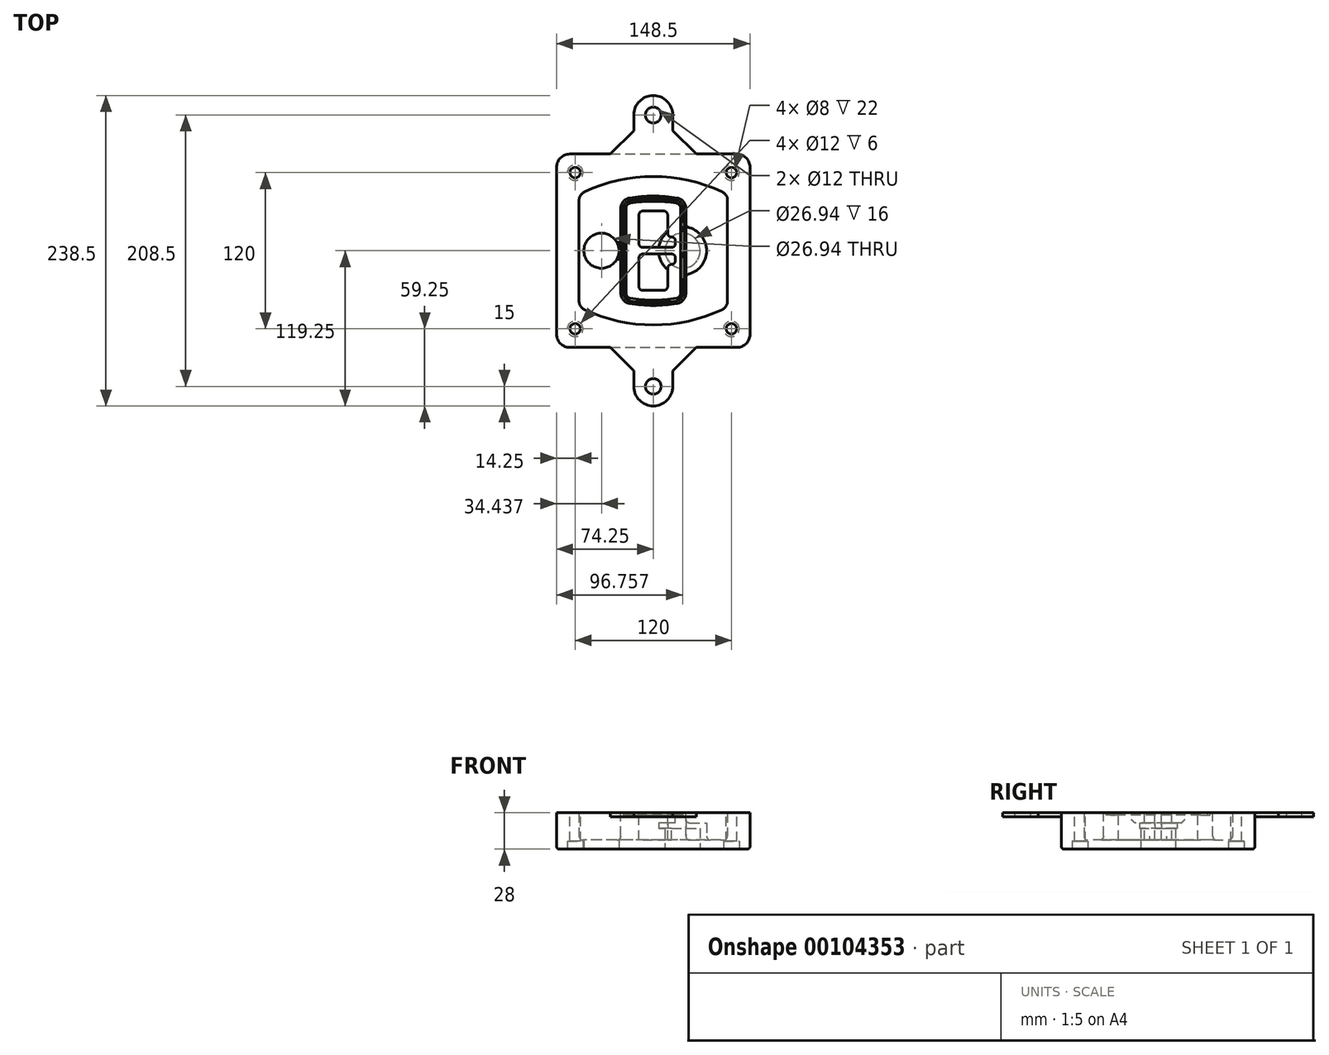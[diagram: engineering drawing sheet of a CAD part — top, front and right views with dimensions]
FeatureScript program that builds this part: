
annotation { "Feature Type Name" : "Feature", "Feature Type Description" : "" }
export const myFeature = defineFeature(function(context is Context, id is Id, definition is map)
    precondition{}
    {
        {
            var Q0;
            Q0=qCreatedBy(makeId("Top.planeOp"),FACE);
            var sketch = newSketch(context, id + "F0", { "sketchPlane" : qUnion([Q0])});
            skPoint(sketch, "E0.rect.middle", {"position": v(0, 0) * mm});
            skLineSegment(sketch, "E1.bottom", {"start": v(-64.25, -74.25) * mm, "end": v(64.25, -74.25) * mm});
            skLineSegment(sketch, "E1.top", {"start": v(-64.25, 74.25) * mm, "end": v(64.25, 74.25) * mm});
            skLineSegment(sketch, "E1.left", {"start": v(-74.25, -64.25) * mm, "end": v(-74.25, 64.25) * mm});
            skLineSegment(sketch, "E1.right", {"start": v(74.25, -64.25) * mm, "end": v(74.25, 64.25) * mm});
            skLineSegment(sketch, "E2", {"start": v(-74.25, 74.25) * mm, "end": v(74.25, -74.25) * mm, "construction": true});
            skLineSegment(sketch, "E3", {"start": v(74.25, 74.25) * mm, "end": v(-74.25, -74.25) * mm, "construction": true});
            skCircle(sketch, "E4", {"center": v(-60, 60) * mm, "radius": 4 * mm});
            skCircle(sketch, "E5", {"center": v(60, 60) * mm, "radius": 4 * mm});
            skCircle(sketch, "E6", {"center": v(60, -60) * mm, "radius": 4 * mm});
            skCircle(sketch, "E7", {"center": v(-60, -60) * mm, "radius": 4 * mm});
            skLineSegment(sketch, "E8", {"start": v(-60, 60) * mm, "end": v(60, 60) * mm, "construction": true});
            skLineSegment(sketch, "E9", {"start": v(60, 60) * mm, "end": v(60, -60) * mm, "construction": true});
            skLineSegment(sketch, "E10", {"start": v(60, -60) * mm, "end": v(-60, -60) * mm, "construction": true});
            skLineSegment(sketch, "E11", {"start": v(-60, -60) * mm, "end": v(-60, 60) * mm, "construction": true});
            skLineSegment(sketch, "E12", {"start": v(-60, 38.83) * mm, "end": v(-60, -38.83) * mm});
            skLineSegment(sketch, "E13", {"start": v(60, 38.83) * mm, "end": v(60, -38.83) * mm});
            skArc(sketch, "E14", {"start": v(54.26, 47.88) * mm, "mid": v(0, 60) * mm, "end": v(-54.26, 47.88) * mm});
            skArc(sketch, "E15", {"start": v(-54.26, -47.88) * mm, "mid": v(0, -60) * mm, "end": v(54.26, -47.88) * mm});
            skLineSegment(sketch, "E16", {"start": v(-60, 0) * mm, "end": v(60, 0) * mm, "construction": true});
            skPoint(sketch, "E17.visualSharp", {"position": v(-60, -45) * mm});
            skArc(sketch, "E17.filletArc", {"start": v(-60, -38.83) * mm, "mid": v(-58.44, -44.2) * mm, "end": v(-54.26, -47.88) * mm});
            skPoint(sketch, "E18.visualSharp", {"position": v(-60, 45) * mm});
            skArc(sketch, "E18.filletArc", {"start": v(-54.26, 47.88) * mm, "mid": v(-58.44, 44.2) * mm, "end": v(-60, 38.83) * mm});
            skPoint(sketch, "E19.visualSharp", {"position": v(60, 45) * mm});
            skArc(sketch, "E19.filletArc", {"start": v(60, 38.83) * mm, "mid": v(58.44, 44.2) * mm, "end": v(54.26, 47.88) * mm});
            skPoint(sketch, "E20.visualSharp", {"position": v(60, -45) * mm});
            skArc(sketch, "E20.filletArc", {"start": v(54.26, -47.88) * mm, "mid": v(58.44, -44.2) * mm, "end": v(60, -38.83) * mm});
            skPoint(sketch, "E21.visualSharp", {"position": v(-74.25, 74.25) * mm});
            skArc(sketch, "E21.filletArc", {"start": v(-64.25, 74.25) * mm, "mid": v(-71.32, 71.32) * mm, "end": v(-74.25, 64.25) * mm});
            skPoint(sketch, "E22.visualSharp", {"position": v(74.25, 74.25) * mm});
            skArc(sketch, "E22.filletArc", {"start": v(74.25, 64.25) * mm, "mid": v(71.32, 71.32) * mm, "end": v(64.25, 74.25) * mm});
            skPoint(sketch, "E23.visualSharp", {"position": v(74.25, -74.25) * mm});
            skArc(sketch, "E23.filletArc", {"start": v(64.25, -74.25) * mm, "mid": v(71.32, -71.32) * mm, "end": v(74.25, -64.25) * mm});
            skPoint(sketch, "E24.visualSharp", {"position": v(-74.25, -74.25) * mm});
            skArc(sketch, "E24.filletArc", {"start": v(-74.25, -64.25) * mm, "mid": v(-71.32, -71.32) * mm, "end": v(-64.25, -74.25) * mm});
            skArc(sketch, "E25.0", {"start": v(57, 38.83) * mm, "mid": v(55.9, 42.58) * mm, "end": v(52.98, 45.17) * mm});
            skLineSegment(sketch, "E25.1", {"start": v(57, 38.83) * mm, "end": v(57, -38.83) * mm});
            skArc(sketch, "E25.2", {"start": v(52.98, -45.17) * mm, "mid": v(55.9, -42.58) * mm, "end": v(57, -38.83) * mm});
            skArc(sketch, "E25.3", {"start": v(-52.98, -45.17) * mm, "mid": v(0, -57) * mm, "end": v(52.98, -45.17) * mm});
            skArc(sketch, "E25.4", {"start": v(-57, -38.83) * mm, "mid": v(-55.9, -42.58) * mm, "end": v(-52.98, -45.17) * mm});
            skArc(sketch, "E25.5", {"start": v(52.98, 45.17) * mm, "mid": v(0, 57) * mm, "end": v(-52.98, 45.17) * mm});
            skLineSegment(sketch, "E25.6", {"start": v(-57, 38.83) * mm, "end": v(-57, -38.83) * mm});
            skArc(sketch, "E25.7", {"start": v(-52.98, 45.17) * mm, "mid": v(-55.9, 42.58) * mm, "end": v(-57, 38.83) * mm});
            skArc(sketch, "E26.0", {"start": v(-55.96, 51.5) * mm, "mid": v(-61.82, 46.33) * mm, "end": v(-64, 38.83) * mm});
            skArc(sketch, "E26.1", {"start": v(55.96, 51.5) * mm, "mid": v(0, 64) * mm, "end": v(-55.96, 51.5) * mm});
            skArc(sketch, "E26.2", {"start": v(64, 38.83) * mm, "mid": v(61.82, 46.33) * mm, "end": v(55.96, 51.5) * mm});
            skLineSegment(sketch, "E26.3", {"start": v(64, 38.83) * mm, "end": v(64, -38.83) * mm});
            skArc(sketch, "E26.4", {"start": v(55.96, -51.5) * mm, "mid": v(61.82, -46.33) * mm, "end": v(64, -38.83) * mm});
            skLineSegment(sketch, "E26.5", {"start": v(-64, 38.83) * mm, "end": v(-64, -38.83) * mm});
            skArc(sketch, "E26.6", {"start": v(-55.96, -51.5) * mm, "mid": v(0, -64) * mm, "end": v(55.96, -51.5) * mm});
            skArc(sketch, "E26.7", {"start": v(-64, -38.83) * mm, "mid": v(-61.82, -46.33) * mm, "end": v(-55.96, -51.5) * mm});
            skSolve(sketch);
        }
        {
            var Q0;
            Q0=makeQuery(id+"F0.imprint","IMPRINT",FACE,{"disambiguationData":[TD([[makeQuery(id+"F0.imprint","IMPRINT",EDGE,{"derivedFrom":sQuery(id+"F0.wireOp",EDGE,"E1.bottom")}),1.0]])]});
            var Q1;
            Q1=makeQuery(id+"F0.imprint","IMPRINT",FACE,{"disambiguationData":[TD([[makeQuery(id+"F0.imprint","IMPRINT",EDGE,{"derivedFrom":sQuery(id+"F0.wireOp",EDGE,"E12")}),1.0]])]});
            var Q2;
            Q2=makeQuery(id+"F0.imprint","IMPRINT",FACE,{"disambiguationData":[TD([[makeQuery(id+"F0.imprint","IMPRINT",EDGE,{"derivedFrom":sQuery(id+"F0.wireOp",EDGE,"E25.0")}),1.0]])]});
            var Q3;
            Q3=makeQuery(id+"F0.imprint","IMPRINT",FACE,{"disambiguationData":[TD([[makeQuery(id+"F0.imprint","IMPRINT",EDGE,{"derivedFrom":sQuery(id+"F0.wireOp",EDGE,"E12")}),-1.0]])]});
            extrude(context, id + "F1", {"entities" : qUnion([Q0, Q1, Q2, Q3]), "oppositeDirection" : true, "depth" : 25 * mm});
        }
        {
            var Q0;
            Q0=makeQuery(id+"F0.imprint","IMPRINT",FACE,{"disambiguationData":[TD([[makeQuery(id+"F0.imprint","IMPRINT",EDGE,{"derivedFrom":sQuery(id+"F0.wireOp",EDGE,"E12")}),1.0]])]});
            extrude(context, id + "F2", {"entities" : qUnion([Q0]), "operationType" : NewBodyOperationType.ADD, "depth" : 3 * mm});
        }
        {
            var Q0;
            Q0=makeQuery(id+"F0.imprint","IMPRINT",FACE,{"disambiguationData":[TD([[makeQuery(id+"F0.imprint","IMPRINT",EDGE,{"derivedFrom":sQuery(id+"F0.wireOp",EDGE,"E25.0")}),1.0]])]});
            extrude(context, id + "F3", {"entities" : qUnion([Q0]), "operationType" : NewBodyOperationType.REMOVE, "oppositeDirection" : true, "depth" : 18 * mm});
        }
        {
            var Q0;
            Q0=makeQuery(id+"F2.opExtrude","CAP_FACE",FACE,{"disambiguationData":[OSD([sQuery(id+"F0.wireOp",EDGE,"E12"),sQuery(id+"F0.wireOp",EDGE,"E13"),sQuery(id+"F0.wireOp",EDGE,"E14"),sQuery(id+"F0.wireOp",EDGE,"E15"),sQuery(id+"F0.wireOp",EDGE,"E17.filletArc"),sQuery(id+"F0.wireOp",EDGE,"E18.filletArc"),sQuery(id+"F0.wireOp",EDGE,"E19.filletArc"),sQuery(id+"F0.wireOp",EDGE,"E20.filletArc"),sQuery(id+"F0.wireOp",EDGE,"E25.0"),sQuery(id+"F0.wireOp",EDGE,"E25.1"),sQuery(id+"F0.wireOp",EDGE,"E25.2"),sQuery(id+"F0.wireOp",EDGE,"E25.3"),sQuery(id+"F0.wireOp",EDGE,"E25.4"),sQuery(id+"F0.wireOp",EDGE,"E25.5"),sQuery(id+"F0.wireOp",EDGE,"E25.6"),sQuery(id+"F0.wireOp",EDGE,"E25.7")])],"isStart":false});
            var sketch = newSketch(context, id + "F4", { "sketchPlane" : qUnion([Q0])});
            skArc(sketch, "E27.0", {"start": v(-18.34, -40.45) * mm, "mid": v(0, -42) * mm, "end": v(18.34, -40.45) * mm});
            skArc(sketch, "E28.0", {"start": v(18.34, 40.45) * mm, "mid": v(0, 42) * mm, "end": v(-18.34, 40.45) * mm});
            skLineSegment(sketch, "E29", {"start": v(-25, 32.57) * mm, "end": v(-25, -32.57) * mm});
            skLineSegment(sketch, "E30", {"start": v(25, 32.57) * mm, "end": v(25, -32.57) * mm});
            skLineSegment(sketch, "E31", {"start": v(-25, 39.1) * mm, "end": v(25, 39.1) * mm, "construction": true});
            skLineSegment(sketch, "E32", {"start": v(-25, -39.1) * mm, "end": v(25, -39.1) * mm, "construction": true});
            skPoint(sketch, "E33.visualSharp", {"position": v(-25, 39.1) * mm});
            skArc(sketch, "E33.filletArc", {"start": v(-18.34, 40.45) * mm, "mid": v(-23.11, 37.73) * mm, "end": v(-25, 32.57) * mm});
            skPoint(sketch, "E34.visualSharp", {"position": v(25, 39.1) * mm});
            skArc(sketch, "E34.filletArc", {"start": v(25, 32.57) * mm, "mid": v(23.11, 37.73) * mm, "end": v(18.34, 40.45) * mm});
            skPoint(sketch, "E35.visualSharp", {"position": v(25, -39.1) * mm});
            skArc(sketch, "E35.filletArc", {"start": v(18.34, -40.45) * mm, "mid": v(23.11, -37.73) * mm, "end": v(25, -32.57) * mm});
            skPoint(sketch, "E36.visualSharp", {"position": v(-25, -39.1) * mm});
            skArc(sketch, "E36.filletArc", {"start": v(-25, -32.57) * mm, "mid": v(-23.11, -37.73) * mm, "end": v(-18.34, -40.45) * mm});
            skArc(sketch, "E37.0", {"start": v(52.98, 45.17) * mm, "mid": v(0, 57) * mm, "end": v(-52.98, 45.17) * mm});
            skArc(sketch, "E37.1", {"start": v(-52.98, 45.17) * mm, "mid": v(-55.9, 42.58) * mm, "end": v(-57, 38.83) * mm});
            skLineSegment(sketch, "E37.2", {"start": v(-57, 38.83) * mm, "end": v(-57, -38.83) * mm});
            skArc(sketch, "E37.3", {"start": v(-57, -38.83) * mm, "mid": v(-55.9, -42.58) * mm, "end": v(-52.98, -45.17) * mm});
            skArc(sketch, "E37.4", {"start": v(-52.98, -45.17) * mm, "mid": v(0, -57) * mm, "end": v(52.98, -45.17) * mm});
            skArc(sketch, "E37.5", {"start": v(52.98, -45.17) * mm, "mid": v(55.9, -42.58) * mm, "end": v(57, -38.83) * mm});
            skLineSegment(sketch, "E37.6", {"start": v(57, 38.83) * mm, "end": v(57, -38.83) * mm});
            skArc(sketch, "E37.7", {"start": v(57, 38.83) * mm, "mid": v(55.9, 42.58) * mm, "end": v(52.98, 45.17) * mm});
            skLineSegment(sketch, "E38.0", {"start": v(23, 32.57) * mm, "end": v(23, -32.57) * mm});
            skArc(sketch, "E38.1", {"start": v(18, -38.48) * mm, "mid": v(21.58, -36.44) * mm, "end": v(23, -32.57) * mm});
            skArc(sketch, "E38.2", {"start": v(-18, -38.48) * mm, "mid": v(0, -40) * mm, "end": v(18, -38.48) * mm});
            skArc(sketch, "E38.3", {"start": v(-23, -32.57) * mm, "mid": v(-21.58, -36.44) * mm, "end": v(-18, -38.48) * mm});
            skLineSegment(sketch, "E38.4", {"start": v(-23, 32.57) * mm, "end": v(-23, -32.57) * mm});
            skArc(sketch, "E38.5", {"start": v(23, 32.57) * mm, "mid": v(21.58, 36.44) * mm, "end": v(18, 38.48) * mm});
            skArc(sketch, "E38.6", {"start": v(-18, 38.48) * mm, "mid": v(-21.58, 36.44) * mm, "end": v(-23, 32.57) * mm});
            skArc(sketch, "E38.7", {"start": v(18, 38.48) * mm, "mid": v(0, 40) * mm, "end": v(-18, 38.48) * mm});
            skArc(sketch, "E39.0", {"start": v(21, 32.57) * mm, "mid": v(20.06, 35.15) * mm, "end": v(17.67, 36.5) * mm});
            skLineSegment(sketch, "E39.1", {"start": v(21, 32.57) * mm, "end": v(21, -32.57) * mm});
            skArc(sketch, "E39.2", {"start": v(17.67, -36.5) * mm, "mid": v(20.06, -35.15) * mm, "end": v(21, -32.57) * mm});
            skArc(sketch, "E39.3", {"start": v(-17.67, -36.5) * mm, "mid": v(0, -38) * mm, "end": v(17.67, -36.5) * mm});
            skArc(sketch, "E39.4", {"start": v(-21, -32.57) * mm, "mid": v(-20.06, -35.15) * mm, "end": v(-17.67, -36.5) * mm});
            skArc(sketch, "E39.5", {"start": v(17.67, 36.5) * mm, "mid": v(0, 38) * mm, "end": v(-17.67, 36.5) * mm});
            skLineSegment(sketch, "E39.6", {"start": v(-21, 32.57) * mm, "end": v(-21, -32.57) * mm});
            skArc(sketch, "E39.7", {"start": v(-17.67, 36.5) * mm, "mid": v(-20.06, 35.15) * mm, "end": v(-21, 32.57) * mm});
            skLineSegment(sketch, "E40", {"start": v(-25, 0) * mm, "end": v(25, 0) * mm, "construction": true});
            skLineSegment(sketch, "E41", {"start": v(-11, 5.5) * mm, "end": v(-11, 27.5) * mm});
            skLineSegment(sketch, "E42", {"start": v(-8, 30.5) * mm, "end": v(8, 30.5) * mm});
            skLineSegment(sketch, "E43", {"start": v(11, 27.5) * mm, "end": v(11, 13.5) * mm});
            skLineSegment(sketch, "E44", {"start": v(14, 10.5) * mm, "end": v(14, 10.5) * mm});
            skLineSegment(sketch, "E45", {"start": v(17, 7.5) * mm, "end": v(17, 5.5) * mm});
            skLineSegment(sketch, "E46", {"start": v(14, 2.5) * mm, "end": v(-8, 2.5) * mm});
            skPoint(sketch, "E47.visualSharp", {"position": v(-11, 30.5) * mm});
            skArc(sketch, "E47.filletArc", {"start": v(-8, 30.5) * mm, "mid": v(-10.12, 29.62) * mm, "end": v(-11, 27.5) * mm});
            skPoint(sketch, "E48.visualSharp", {"position": v(11, 30.5) * mm});
            skArc(sketch, "E48.filletArc", {"start": v(11, 27.5) * mm, "mid": v(10.12, 29.62) * mm, "end": v(8, 30.5) * mm});
            skPoint(sketch, "E49.visualSharp", {"position": v(11, 10.5) * mm});
            skArc(sketch, "E49.filletArc", {"start": v(11, 13.5) * mm, "mid": v(11.88, 11.38) * mm, "end": v(14, 10.5) * mm});
            skPoint(sketch, "E50.visualSharp", {"position": v(17, 10.5) * mm});
            skArc(sketch, "E50.filletArc", {"start": v(17, 7.5) * mm, "mid": v(16.12, 9.62) * mm, "end": v(14, 10.5) * mm});
            skPoint(sketch, "E51.visualSharp", {"position": v(17, 2.5) * mm});
            skArc(sketch, "E51.filletArc", {"start": v(14, 2.5) * mm, "mid": v(16.12, 3.38) * mm, "end": v(17, 5.5) * mm});
            skPoint(sketch, "E52.visualSharp", {"position": v(-11, 2.5) * mm});
            skArc(sketch, "E52.filletArc", {"start": v(-11, 5.5) * mm, "mid": v(-10.12, 3.38) * mm, "end": v(-8, 2.5) * mm});
            skLineSegment(sketch, "E53.0.MirrorCS", {"start": v(14, -2.5) * mm, "end": v(-8, -2.5) * mm});
            skArc(sketch, "E54.0.MirrorCS", {"start": v(-11, -5.5) * mm, "mid": v(-10.12, -3.38) * mm, "end": v(-8, -2.5) * mm});
            skLineSegment(sketch, "E55.0.MirrorCS", {"start": v(-11, -5.5) * mm, "end": v(-11, -27.5) * mm});
            skArc(sketch, "E56.0.MirrorCS", {"start": v(-8, -30.5) * mm, "mid": v(-10.12, -29.62) * mm, "end": v(-11, -27.5) * mm});
            skLineSegment(sketch, "E57.0.MirrorCS", {"start": v(-8, -30.5) * mm, "end": v(8, -30.5) * mm});
            skArc(sketch, "E58.0.MirrorCS", {"start": v(11, -27.5) * mm, "mid": v(10.12, -29.62) * mm, "end": v(8, -30.5) * mm});
            skLineSegment(sketch, "E59.0.MirrorCS", {"start": v(11, -27.5) * mm, "end": v(11, -13.5) * mm});
            skArc(sketch, "E60.0.MirrorCS", {"start": v(11, -13.5) * mm, "mid": v(11.88, -11.38) * mm, "end": v(14, -10.5) * mm});
            skArc(sketch, "E61.0.MirrorCS", {"start": v(17, -7.5) * mm, "mid": v(16.12, -9.62) * mm, "end": v(14, -10.5) * mm});
            skLineSegment(sketch, "E62.0.MirrorCS", {"start": v(17, -7.5) * mm, "end": v(17, -5.5) * mm});
            skArc(sketch, "E63.0.MirrorCS", {"start": v(14, -2.5) * mm, "mid": v(16.12, -3.38) * mm, "end": v(17, -5.5) * mm});
            skSolve(sketch);
        }
        {
            var Q0;
            Q0=makeQuery(id+"F4.imprint","IMPRINT",FACE,{"disambiguationData":[TD([[makeQuery(id+"F4.imprint","IMPRINT",EDGE,{"derivedFrom":sQuery(id+"F4.wireOp",EDGE,"E27.0")}),1.0]])]});
            var Q1;
            Q1=makeQuery(id+"F4.imprint","IMPRINT",FACE,{"disambiguationData":[TD([[makeQuery(id+"F4.imprint","IMPRINT",EDGE,{"derivedFrom":sQuery(id+"F4.wireOp",EDGE,"E38.0")}),-1.0]])]});
            var Q2;
            Q2=makeQuery(id+"F4.imprint","IMPRINT",FACE,{"disambiguationData":[TD([[makeQuery(id+"F4.imprint","IMPRINT",EDGE,{"derivedFrom":sQuery(id+"F4.wireOp",EDGE,"E39.0")}),1.0]])]});
            extrude(context, id + "F5", {"entities" : qUnion([Q0, Q1, Q2]), "operationType" : NewBodyOperationType.ADD, "endBound" : BoundingType.UP_TO_NEXT, "oppositeDirection" : true, "depth" : 25 * mm});
        }
        {
            var Q0;
            Q0=makeQuery(id+"F4.imprint","IMPRINT",FACE,{"disambiguationData":[TD([[makeQuery(id+"F4.imprint","IMPRINT",EDGE,{"derivedFrom":sQuery(id+"F4.wireOp",EDGE,"E38.0")}),-1.0]])]});
            extrude(context, id + "F6", {"entities" : qUnion([Q0]), "operationType" : NewBodyOperationType.REMOVE, "oppositeDirection" : true, "depth" : 2 * mm});
        }
        {
            var Q0;
            Q0=makeQuery(id+"F1.opExtrude","CAP_FACE",FACE,{"disambiguationData":[OSD([sQuery(id+"F0.wireOp",EDGE,"E1.bottom"),sQuery(id+"F0.wireOp",EDGE,"E1.top"),sQuery(id+"F0.wireOp",EDGE,"E1.left"),sQuery(id+"F0.wireOp",EDGE,"E1.right"),sQuery(id+"F0.wireOp",EDGE,"E4"),sQuery(id+"F0.wireOp",EDGE,"E5"),sQuery(id+"F0.wireOp",EDGE,"E6"),sQuery(id+"F0.wireOp",EDGE,"E7"),sQuery(id+"F0.wireOp",EDGE,"E21.filletArc"),sQuery(id+"F0.wireOp",EDGE,"E22.filletArc"),sQuery(id+"F0.wireOp",EDGE,"E23.filletArc"),sQuery(id+"F0.wireOp",EDGE,"E24.filletArc")])],"isStart":false});
            var sketch = newSketch(context, id + "F7", { "sketchPlane" : qUnion([Q0])});
            skCircle(sketch, "E64", {"center": v(22.5, 0) * mm, "radius": 13.47 * mm});
            skCircle(sketch, "E65", {"center": v(-39.81, 0) * mm, "radius": 13.47 * mm});
            skLineSegment(sketch, "E66", {"start": v(74.25, 0) * mm, "end": v(-74.25, 0) * mm});
            skCircle(sketch, "E67", {"center": v(22.5, 0) * mm, "radius": 18.47 * mm});
            skCircle(sketch, "E68", {"center": v(60, -60) * mm, "radius": 6 * mm});
            skCircle(sketch, "E69", {"center": v(-60, -60) * mm, "radius": 6 * mm});
            skCircle(sketch, "E70", {"center": v(-60, 60) * mm, "radius": 6 * mm});
            skCircle(sketch, "E71", {"center": v(60, 60) * mm, "radius": 6 * mm});
            skSolve(sketch);
        }
        {
            var Q0;
            {var subQ1=sQuery(id+"F7.wireOp",EDGE,"E66");var subQ4=sQuery(id+"F7.wireOp",EDGE,"E64");var subQ6=makeQuery(id+"F7.imprint","INTERSECT",VERTEX,{"disambiguationData":[OD(0.0)],"derivedFrom":[subQ4,subQ1]});Q0=makeQuery(id+"F7.imprint","IMPRINT",FACE,{"disambiguationData":[TD([[makeQuery(id+"F7.imprint","IMPRINT",EDGE,{"disambiguationData":[TD([[subQ6,-1.0]])],"derivedFrom":subQ4}),-1.0]])]});}
            var Q1;
            {var subQ0=sQuery(id+"F7.wireOp",EDGE,"E66");var subQ1=sQuery(id+"F7.wireOp",EDGE,"E64");var subQ3=makeQuery(id+"F7.imprint","INTERSECT",VERTEX,{"disambiguationData":[OD(0.0)],"derivedFrom":[subQ1,subQ0]});Q1=makeQuery(id+"F7.imprint","IMPRINT",FACE,{"disambiguationData":[TD([[makeQuery(id+"F7.imprint","IMPRINT",EDGE,{"disambiguationData":[TD([[subQ3,-1.0]])],"derivedFrom":subQ1}),1.0]])]});}
            var Q2;
            {var subQ0=sQuery(id+"F7.wireOp",EDGE,"E66");var subQ1=sQuery(id+"F7.wireOp",EDGE,"E64");var subQ3=makeQuery(id+"F7.imprint","INTERSECT",VERTEX,{"disambiguationData":[OD(0.0)],"derivedFrom":[subQ1,subQ0]});Q2=makeQuery(id+"F7.imprint","IMPRINT",FACE,{"disambiguationData":[TD([[makeQuery(id+"F7.imprint","IMPRINT",EDGE,{"disambiguationData":[TD([[subQ3,1.0]])],"derivedFrom":subQ1}),1.0]])]});}
            var Q3;
            {var subQ1=sQuery(id+"F7.wireOp",EDGE,"E66");var subQ4=sQuery(id+"F7.wireOp",EDGE,"E64");var subQ6=makeQuery(id+"F7.imprint","INTERSECT",VERTEX,{"disambiguationData":[OD(0.0)],"derivedFrom":[subQ4,subQ1]});Q3=makeQuery(id+"F7.imprint","IMPRINT",FACE,{"disambiguationData":[TD([[makeQuery(id+"F7.imprint","IMPRINT",EDGE,{"disambiguationData":[TD([[subQ6,1.0]])],"derivedFrom":subQ4}),-1.0]])]});}
            extrude(context, id + "F8", {"entities" : qUnion([Q0, Q1, Q2, Q3]), "operationType" : NewBodyOperationType.ADD, "oppositeDirection" : true, "depth" : 20 * mm});
        }
        {
            var Q0;
            {var subQ0=sQuery(id+"F7.wireOp",EDGE,"E66");var subQ1=sQuery(id+"F7.wireOp",EDGE,"E64");var subQ3=makeQuery(id+"F7.imprint","INTERSECT",VERTEX,{"disambiguationData":[OD(0.0)],"derivedFrom":[subQ1,subQ0]});Q0=makeQuery(id+"F7.imprint","IMPRINT",FACE,{"disambiguationData":[TD([[makeQuery(id+"F7.imprint","IMPRINT",EDGE,{"disambiguationData":[TD([[subQ3,-1.0]])],"derivedFrom":subQ1}),1.0]])]});}
            var Q1;
            {var subQ0=sQuery(id+"F7.wireOp",EDGE,"E66");var subQ1=sQuery(id+"F7.wireOp",EDGE,"E64");var subQ3=makeQuery(id+"F7.imprint","INTERSECT",VERTEX,{"disambiguationData":[OD(0.0)],"derivedFrom":[subQ1,subQ0]});Q1=makeQuery(id+"F7.imprint","IMPRINT",FACE,{"disambiguationData":[TD([[makeQuery(id+"F7.imprint","IMPRINT",EDGE,{"disambiguationData":[TD([[subQ3,1.0]])],"derivedFrom":subQ1}),1.0]])]});}
            extrude(context, id + "F9", {"entities" : qUnion([Q0, Q1]), "operationType" : NewBodyOperationType.REMOVE, "oppositeDirection" : true, "depth" : 16 * mm});
        }
        {
            var Q0;
            {var subQ0=sQuery(id+"F7.wireOp",EDGE,"E66");var subQ1=sQuery(id+"F7.wireOp",EDGE,"E65");var subQ3=makeQuery(id+"F7.imprint","INTERSECT",VERTEX,{"disambiguationData":[OD(0.0)],"derivedFrom":[subQ1,subQ0]});Q0=makeQuery(id+"F7.imprint","IMPRINT",FACE,{"disambiguationData":[TD([[makeQuery(id+"F7.imprint","IMPRINT",EDGE,{"disambiguationData":[TD([[subQ3,-1.0]])],"derivedFrom":subQ1}),1.0]])]});}
            var Q1;
            {var subQ0=sQuery(id+"F7.wireOp",EDGE,"E66");var subQ1=sQuery(id+"F7.wireOp",EDGE,"E65");var subQ3=makeQuery(id+"F7.imprint","INTERSECT",VERTEX,{"disambiguationData":[OD(0.0)],"derivedFrom":[subQ1,subQ0]});Q1=makeQuery(id+"F7.imprint","IMPRINT",FACE,{"disambiguationData":[TD([[makeQuery(id+"F7.imprint","IMPRINT",EDGE,{"disambiguationData":[TD([[subQ3,1.0]])],"derivedFrom":subQ1}),1.0]])]});}
            extrude(context, id + "F10", {"entities" : qUnion([Q0, Q1]), "operationType" : NewBodyOperationType.REMOVE, "oppositeDirection" : true, "depth" : 25 * mm});
        }
        {
            var Q0;
            Q0=makeQuery(id+"F7.imprint","IMPRINT",FACE,{"disambiguationData":[TD([[makeQuery(id+"F7.imprint","IMPRINT",EDGE,{"derivedFrom":sQuery(id+"F7.wireOp",EDGE,"E68")}),1.0]])]});
            var Q1;
            Q1=makeQuery(id+"F7.imprint","IMPRINT",FACE,{"disambiguationData":[TD([[makeQuery(id+"F7.imprint","IMPRINT",EDGE,{"derivedFrom":makeQuery(id+"F1.opExtrude","CAP_EDGE",EDGE,{"disambiguationData":[OSD([sQuery(id+"F0.wireOp",EDGE,"E5")])],"isStart":false})}),-1.0]])]});
            var Q2;
            Q2=makeQuery(id+"F7.imprint","IMPRINT",FACE,{"disambiguationData":[TD([[makeQuery(id+"F7.imprint","IMPRINT",EDGE,{"derivedFrom":sQuery(id+"F7.wireOp",EDGE,"E69")}),1.0]])]});
            var Q3;
            Q3=makeQuery(id+"F7.imprint","IMPRINT",FACE,{"disambiguationData":[TD([[makeQuery(id+"F7.imprint","IMPRINT",EDGE,{"derivedFrom":makeQuery(id+"F1.opExtrude","CAP_EDGE",EDGE,{"disambiguationData":[OSD([sQuery(id+"F0.wireOp",EDGE,"E4")])],"isStart":false})}),-1.0]])]});
            var Q4;
            Q4=makeQuery(id+"F7.imprint","IMPRINT",FACE,{"disambiguationData":[TD([[makeQuery(id+"F7.imprint","IMPRINT",EDGE,{"derivedFrom":sQuery(id+"F7.wireOp",EDGE,"E70")}),1.0]])]});
            var Q5;
            Q5=makeQuery(id+"F7.imprint","IMPRINT",FACE,{"disambiguationData":[TD([[makeQuery(id+"F7.imprint","IMPRINT",EDGE,{"derivedFrom":makeQuery(id+"F1.opExtrude","CAP_EDGE",EDGE,{"disambiguationData":[OSD([sQuery(id+"F0.wireOp",EDGE,"E7")])],"isStart":false})}),-1.0]])]});
            var Q6;
            Q6=makeQuery(id+"F7.imprint","IMPRINT",FACE,{"disambiguationData":[TD([[makeQuery(id+"F7.imprint","IMPRINT",EDGE,{"derivedFrom":sQuery(id+"F7.wireOp",EDGE,"E71")}),1.0]])]});
            var Q7;
            Q7=makeQuery(id+"F7.imprint","IMPRINT",FACE,{"disambiguationData":[TD([[makeQuery(id+"F7.imprint","IMPRINT",EDGE,{"derivedFrom":makeQuery(id+"F1.opExtrude","CAP_EDGE",EDGE,{"disambiguationData":[OSD([sQuery(id+"F0.wireOp",EDGE,"E6")])],"isStart":false})}),-1.0]])]});
            extrude(context, id + "F11", {"entities" : qUnion([Q0, Q1, Q2, Q3, Q4, Q5, Q6, Q7]), "operationType" : NewBodyOperationType.REMOVE, "oppositeDirection" : true, "depth" : 6 * mm});
        }
        {
            var Q0;
            Q0=makeQuery(id+"F9.boolean.opBoolean","COPY",FACE,{"derivedFrom":makeQuery(id+"F9.opExtrude","CAP_FACE",FACE,{"disambiguationData":[OSD([sQuery(id+"F7.wireOp",EDGE,"E64")])],"isStart":false})});
            var sketch = newSketch(context, id + "F12", { "sketchPlane" : qUnion([Q0])});
            skArc(sketch, "E72.0", {"start": v(11, 14.45) * mm, "mid": v(6.45, 9.13) * mm, "end": v(4.2, 2.5) * mm});
            skArc(sketch, "E72.1", {"start": v(4.2, -2.5) * mm, "mid": v(6.45, -9.13) * mm, "end": v(11, -14.45) * mm});
            skLineSegment(sketch, "E73", {"start": v(4.2, -2.5) * mm, "end": v(14, -2.5) * mm});
            skLineSegment(sketch, "E74.0", {"start": v(14, 2.5) * mm, "end": v(4.2, 2.5) * mm});
            skArc(sketch, "E74.1", {"start": v(14, 2.5) * mm, "mid": v(16.12, 3.38) * mm, "end": v(17, 5.5) * mm});
            skLineSegment(sketch, "E74.2", {"start": v(17, 7.5) * mm, "end": v(17, 5.5) * mm});
            skArc(sketch, "E74.3", {"start": v(17, 7.5) * mm, "mid": v(16.12, 9.62) * mm, "end": v(14, 10.5) * mm});
            skArc(sketch, "E74.4", {"start": v(11, 13.5) * mm, "mid": v(11.88, 11.38) * mm, "end": v(14, 10.5) * mm});
            skLineSegment(sketch, "E74.5", {"start": v(11, 14.45) * mm, "end": v(11, 13.5) * mm});
            skLineSegment(sketch, "E74.7", {"start": v(14, -2.5) * mm, "end": v(4.2, -2.5) * mm});
            skArc(sketch, "E74.8", {"start": v(14, -2.5) * mm, "mid": v(16.12, -3.38) * mm, "end": v(17, -5.5) * mm});
            skLineSegment(sketch, "E74.9", {"start": v(17, -7.5) * mm, "end": v(17, -5.5) * mm});
            skArc(sketch, "E74.10", {"start": v(17, -7.5) * mm, "mid": v(16.12, -9.62) * mm, "end": v(14, -10.5) * mm});
            skArc(sketch, "E74.11", {"start": v(11, -13.5) * mm, "mid": v(11.88, -11.38) * mm, "end": v(14, -10.5) * mm});
            skLineSegment(sketch, "E74.12", {"start": v(11, -14.45) * mm, "end": v(11, -13.5) * mm});
            skPoint(sketch, "E75.orphan", {"position": v(11, -27.5) * mm});
            skPoint(sketch, "E76.orphan", {"position": v(-8, -2.5) * mm});
            skPoint(sketch, "E77.orphan", {"position": v(-8, 2.5) * mm});
            skPoint(sketch, "E78.orphan", {"position": v(11, 27.5) * mm});
            skSolve(sketch);
        }
        {
            var Q0;
            {var subQ7=sQuery(id+"F12.wireOp",EDGE,"E72.0");var subQ14=sQuery(id+"F12.wireOp",EDGE,"E72.1");var subQ16=sQuery(id+"F12.wireOp",EDGE,"E74.1");var subQ18=sQuery(id+"F12.wireOp",EDGE,"E74.8");Q0=qUnion([makeQuery(id+"F12.imprint","IMPRINT",FACE,{"disambiguationData":[TD([[makeQuery(id+"F12.imprint","IMPRINT",EDGE,{"derivedFrom":subQ7}),1.0]])]}),makeQuery(id+"F12.imprint","IMPRINT",FACE,{"disambiguationData":[TD([[makeQuery(id+"F12.imprint","IMPRINT",EDGE,{"derivedFrom":subQ14}),1.0]])]}),makeQuery(id+"F12.imprint","IMPRINT",FACE,{"disambiguationData":[TD([[makeQuery(id+"F12.imprint","IMPRINT",EDGE,{"derivedFrom":subQ16}),1.0]])]}),makeQuery(id+"F12.imprint","IMPRINT",FACE,{"disambiguationData":[TD([[makeQuery(id+"F12.imprint","IMPRINT",EDGE,{"derivedFrom":subQ18}),-1.0]])]})]);}
            var Q1;
            Q1=makeQuery(id+"F5.boolean.opBoolean","SPLIT",FACE,{"disambiguationData":[TD([makeQuery(id+"F5.opExtrude","SWEPT_FACE",FACE,{"disambiguationData":[OSD([sQuery(id+"F4.wireOp",EDGE,"E41")])]})])],"derivedFrom":makeQuery(id+"F3.boolean.opBoolean","COPY",FACE,{"derivedFrom":makeQuery(id+"F3.opExtrude","CAP_FACE",FACE,{"disambiguationData":[OSD([sQuery(id+"F0.wireOp",EDGE,"E25.0"),sQuery(id+"F0.wireOp",EDGE,"E25.1"),sQuery(id+"F0.wireOp",EDGE,"E25.2"),sQuery(id+"F0.wireOp",EDGE,"E25.3"),sQuery(id+"F0.wireOp",EDGE,"E25.4"),sQuery(id+"F0.wireOp",EDGE,"E25.5"),sQuery(id+"F0.wireOp",EDGE,"E25.6"),sQuery(id+"F0.wireOp",EDGE,"E25.7")])],"isStart":false})})});
            extrude(context, id + "F13", {"entities" : qUnion([Q0]), "operationType" : NewBodyOperationType.REMOVE, "endBound" : BoundingType.UP_TO_SURFACE, "endBoundEntityFace" : qUnion([Q1]), "depth" : 25 * mm});
        }
        {
            var Q0;
            Q0=makeQuery(id+"F3.boolean.opBoolean","COPY",EDGE,{"derivedFrom":makeQuery(id+"F3.opExtrude","CAP_EDGE",EDGE,{"disambiguationData":[OSD([sQuery(id+"F0.wireOp",EDGE,"E25.6")])],"isStart":false})});
            var Q1;
            Q1=makeQuery(id+"F8.boolean.opBoolean","INTERSECT",EDGE,{"derivedFrom":[makeQuery(id+"F5.opExtrude","SWEPT_FACE",FACE,{"disambiguationData":[OSD([sQuery(id+"F4.wireOp",EDGE,"E30")])]}),makeQuery(id+"F8.opExtrude","CAP_FACE",FACE,{"disambiguationData":[OSD([sQuery(id+"F7.wireOp",EDGE,"E67")])],"isStart":false})]});
            var Q2;
            Q2=makeQuery(id+"F8.boolean.opBoolean","INTERSECT",EDGE,{"disambiguationData":[OD(1.0)],"derivedFrom":[makeQuery(id+"F5.opExtrude","SWEPT_FACE",FACE,{"disambiguationData":[OSD([sQuery(id+"F4.wireOp",EDGE,"E30")])]}),makeQuery(id+"F8.opExtrude","SWEPT_FACE",FACE,{"disambiguationData":[OSD([sQuery(id+"F7.wireOp",EDGE,"E67")])]})]});
            var Q3;
            {var subQ0=sQuery(id+"F4.wireOp",EDGE,"E30");Q3=makeQuery(id+"F8.boolean.opBoolean","SPLIT",EDGE,{"disambiguationData":[TD([makeQuery(id+"F5.opExtrude","SWEPT_FACE",FACE,{"disambiguationData":[OSD([sQuery(id+"F4.wireOp",EDGE,"E35.filletArc")])]})])],"derivedFrom":makeQuery(id+"F5.opExtrude","CAP_EDGE",EDGE,{"disambiguationData":[OSD([subQ0])],"isStart":false})});}
            var Q4;
            {var subQ0=sQuery(id+"F0.wireOp",EDGE,"E25.7");var subQ1=sQuery(id+"F0.wireOp",EDGE,"E25.1");var subQ2=sQuery(id+"F0.wireOp",EDGE,"E25.6");var subQ3=sQuery(id+"F0.wireOp",EDGE,"E25.5");var subQ4=sQuery(id+"F0.wireOp",EDGE,"E25.4");var subQ5=sQuery(id+"F0.wireOp",EDGE,"E25.0");var subQ6=sQuery(id+"F0.wireOp",EDGE,"E25.2");var subQ7=sQuery(id+"F0.wireOp",EDGE,"E25.3");Q4=makeQuery(id+"F8.boolean.opBoolean","INTERSECT",EDGE,{"derivedFrom":[makeQuery(id+"F5.boolean.opBoolean","SPLIT",FACE,{"disambiguationData":[TD([makeQuery(id+"F2.opExtrude","SWEPT_FACE",FACE,{"disambiguationData":[OSD([subQ5])]})])],"derivedFrom":makeQuery(id+"F3.boolean.opBoolean","COPY",FACE,{"derivedFrom":makeQuery(id+"F3.opExtrude","CAP_FACE",FACE,{"disambiguationData":[OSD([subQ5,subQ1,subQ6,subQ7,subQ4,subQ3,subQ2,subQ0])],"isStart":false})})}),makeQuery(id+"F8.opExtrude","SWEPT_FACE",FACE,{"disambiguationData":[OSD([sQuery(id+"F7.wireOp",EDGE,"E67")])]})]});}
            var Q5;
            Q5=makeQuery(id+"F8.boolean.opBoolean","INTERSECT",EDGE,{"disambiguationData":[OD(0.0)],"derivedFrom":[makeQuery(id+"F5.opExtrude","SWEPT_FACE",FACE,{"disambiguationData":[OSD([sQuery(id+"F4.wireOp",EDGE,"E30")])]}),makeQuery(id+"F8.opExtrude","SWEPT_FACE",FACE,{"disambiguationData":[OSD([sQuery(id+"F7.wireOp",EDGE,"E67")])]})]});
            fillet(context, id + "F14", {"entities" : qUnion([Q0, Q1, Q2, Q3, Q4, Q5]), "radius" : 3 * mm, "tangentPropagation" : true, "allowEdgeOverflow" : false});
        }
        {
            var Q0;
            Q0=makeQuery(id+"F1.opExtrude","CAP_EDGE",EDGE,{"disambiguationData":[OSD([sQuery(id+"F0.wireOp",EDGE,"E1.bottom")])],"isStart":false});
            fillet(context, id + "F15", {"entities" : qUnion([Q0]), "radius" : 2 * mm, "tangentPropagation" : true, "allowEdgeOverflow" : false});
        }
        {
            var Q0;
            {var subQ0=sQuery(id+"F0.wireOp",EDGE,"E22.filletArc");var subQ1=sQuery(id+"F0.wireOp",EDGE,"E7");var subQ2=sQuery(id+"F0.wireOp",EDGE,"E6");var subQ3=sQuery(id+"F0.wireOp",EDGE,"E5");var subQ4=sQuery(id+"F0.wireOp",EDGE,"E4");var subQ5=sQuery(id+"F0.wireOp",EDGE,"E1.bottom");var subQ6=sQuery(id+"F0.wireOp",EDGE,"E21.filletArc");var subQ7=sQuery(id+"F0.wireOp",EDGE,"E1.top");var subQ8=sQuery(id+"F0.wireOp",EDGE,"E1.left");var subQ9=sQuery(id+"F0.wireOp",EDGE,"E1.right");var subQ10=sQuery(id+"F0.wireOp",EDGE,"E23.filletArc");var subQ11=sQuery(id+"F0.wireOp",EDGE,"E24.filletArc");Q0=makeQuery(id+"F2.boolean.opBoolean","SPLIT",FACE,{"disambiguationData":[TD([makeQuery(id+"F1.opExtrude","SWEPT_FACE",FACE,{"disambiguationData":[OSD([subQ5])]})])],"derivedFrom":makeQuery(id+"F1.opExtrude","CAP_FACE",FACE,{"disambiguationData":[OSD([subQ5,subQ7,subQ8,subQ9,subQ4,subQ3,subQ2,subQ1,subQ6,subQ0,subQ10,subQ11])],"isStart":true})});}
            var sketch = newSketch(context, id + "F16", { "sketchPlane" : qUnion([Q0])});
            skLineSegment(sketch, "E79", {"start": v(0, 74.25) * mm, "end": v(0, 104.25) * mm, "construction": true});
            skCircle(sketch, "E80", {"center": v(0, 104.25) * mm, "radius": 6 * mm});
            skLineSegment(sketch, "E81", {"start": v(-33, 74.25) * mm, "end": v(-15, 92.25) * mm});
            skLineSegment(sketch, "E82", {"start": v(-15, 92.25) * mm, "end": v(-15, 104.25) * mm});
            skArc(sketch, "E83", {"start": v(15, 104.25) * mm, "mid": v(0, 119.25) * mm, "end": v(-15, 104.25) * mm});
            skLineSegment(sketch, "E84", {"start": v(15, 104.25) * mm, "end": v(15, 92.25) * mm});
            skLineSegment(sketch, "E85", {"start": v(15, 92.25) * mm, "end": v(33, 74.25) * mm});
            skLineSegment(sketch, "E86", {"start": v(-74.25, 0) * mm, "end": v(74.25, 0) * mm, "construction": true});
            skLineSegment(sketch, "E87.MirrorCS", {"start": v(-33, -74.25) * mm, "end": v(-15, -92.25) * mm});
            skLineSegment(sketch, "E88.MirrorCS", {"start": v(-15, -92.25) * mm, "end": v(-15, -104.25) * mm});
            skArc(sketch, "E89.MirrorCS", {"start": v(15, -104.25) * mm, "mid": v(0, -119.25) * mm, "end": v(-15, -104.25) * mm});
            skLineSegment(sketch, "E90.MirrorCS", {"start": v(15, -104.25) * mm, "end": v(15, -92.25) * mm});
            skLineSegment(sketch, "E91.MirrorCS", {"start": v(15, -92.25) * mm, "end": v(33, -74.25) * mm});
            skCircle(sketch, "E92.MirrorC", {"center": v(0, -104.25) * mm, "radius": 6 * mm});
            skSolve(sketch);
        }
        {
            var Q0;
            {var subQ0=sQuery(id+"F16.wireOp",EDGE,"E87.MirrorCS");Q0=makeQuery(id+"F16.imprint","IMPRINT",FACE,{"disambiguationData":[TD([[makeQuery(id+"F16.imprint","IMPRINT",EDGE,{"derivedFrom":subQ0}),1.0]])]});}
            var Q1;
            Q1=makeQuery(id+"F16.imprint","IMPRINT",FACE,{"disambiguationData":[TD([[makeQuery(id+"F16.imprint","IMPRINT",EDGE,{"derivedFrom":sQuery(id+"F16.wireOp",EDGE,"E80")}),-1.0]])]});
            var Q2;
            Q2=makeQuery(id+"F16.imprint","IMPRINT",FACE,{"disambiguationData":[TD([[makeQuery(id+"F16.imprint","IMPRINT",EDGE,{"derivedFrom":makeQuery(id+"F1.opExtrude","CAP_EDGE",EDGE,{"disambiguationData":[OSD([sQuery(id+"F0.wireOp",EDGE,"E1.left")])],"isStart":true})}),-1.0]])]});
            var Q3;
            Q3=makeQuery(id+"F2.opExtrude","CAP_FACE",FACE,{"disambiguationData":[OSD([sQuery(id+"F0.wireOp",EDGE,"E12"),sQuery(id+"F0.wireOp",EDGE,"E13"),sQuery(id+"F0.wireOp",EDGE,"E14"),sQuery(id+"F0.wireOp",EDGE,"E15"),sQuery(id+"F0.wireOp",EDGE,"E17.filletArc"),sQuery(id+"F0.wireOp",EDGE,"E18.filletArc"),sQuery(id+"F0.wireOp",EDGE,"E19.filletArc"),sQuery(id+"F0.wireOp",EDGE,"E20.filletArc"),sQuery(id+"F0.wireOp",EDGE,"E25.0"),sQuery(id+"F0.wireOp",EDGE,"E25.1"),sQuery(id+"F0.wireOp",EDGE,"E25.2"),sQuery(id+"F0.wireOp",EDGE,"E25.3"),sQuery(id+"F0.wireOp",EDGE,"E25.4"),sQuery(id+"F0.wireOp",EDGE,"E25.5"),sQuery(id+"F0.wireOp",EDGE,"E25.6"),sQuery(id+"F0.wireOp",EDGE,"E25.7")])],"isStart":false});
            extrude(context, id + "F17", {"entities" : qUnion([Q0, Q1, Q2]), "operationType" : NewBodyOperationType.ADD, "endBound" : BoundingType.UP_TO_SURFACE, "endBoundEntityFace" : qUnion([Q3]), "depth" : 25 * mm});
        }
    });
